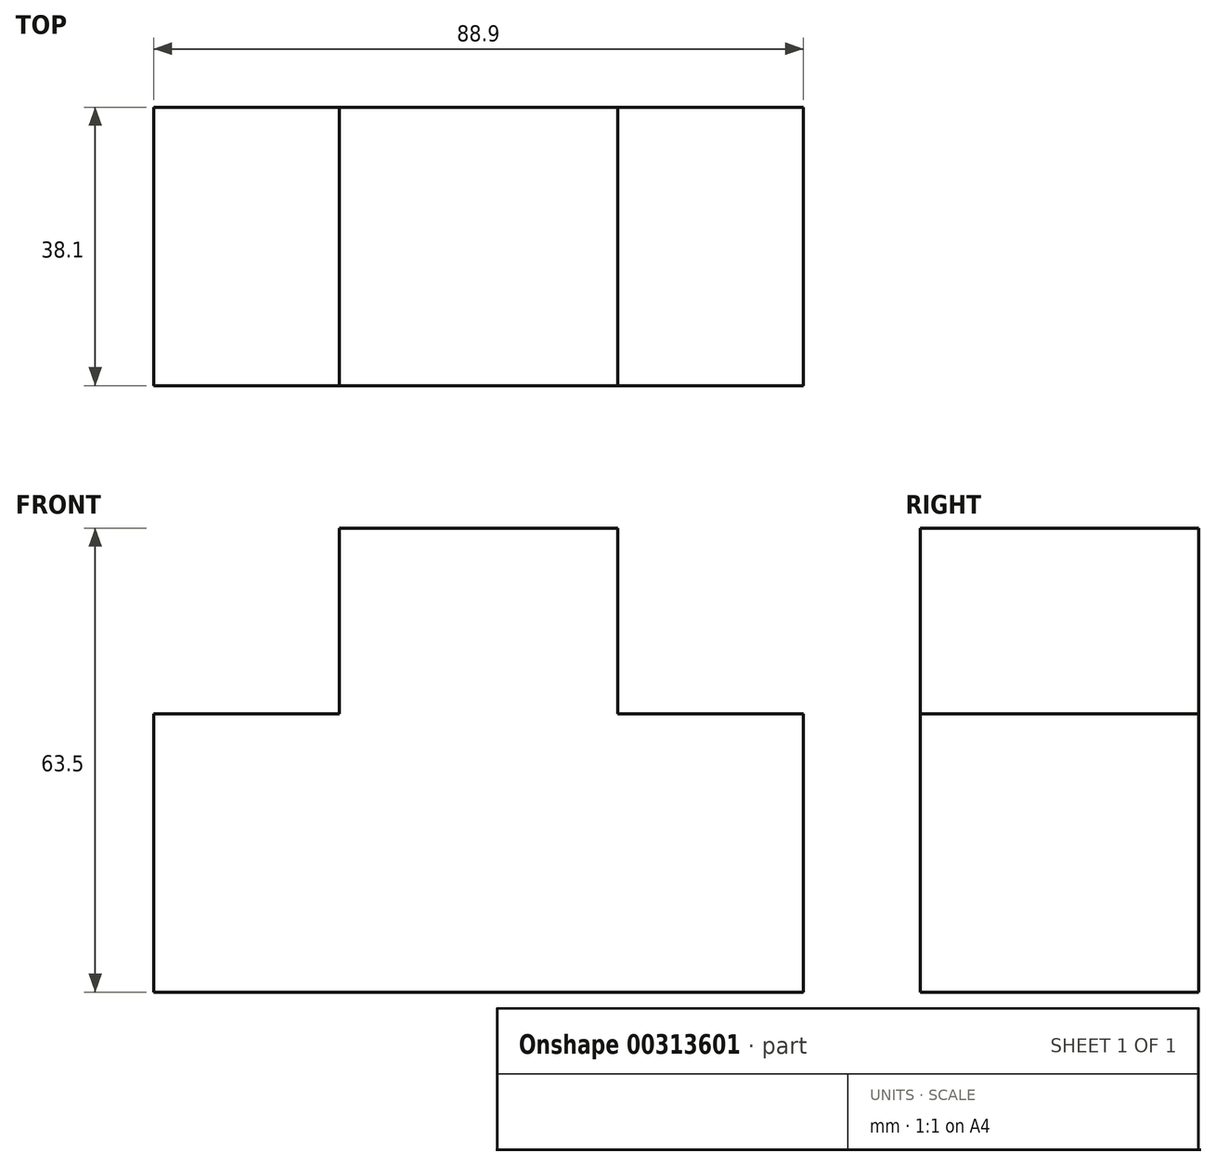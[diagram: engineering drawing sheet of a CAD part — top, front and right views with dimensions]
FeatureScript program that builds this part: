
annotation { "Feature Type Name" : "Feature", "Feature Type Description" : "" }
export const myFeature = defineFeature(function(context is Context, id is Id, definition is map)
    precondition{}
    {
        {
            var Q0;
            Q0=qCreatedBy(makeId("Front.planeOp"),FACE);
            var sketch = newSketch(context, id + "F0", { "sketchPlane" : qUnion([Q0])});
            skLineSegment(sketch, "E0", {"start": v(-52.82, -43.98) * mm, "end": v(36.08, -43.98) * mm});
            skLineSegment(sketch, "E1", {"start": v(36.08, -43.98) * mm, "end": v(36.08, -5.88) * mm});
            skLineSegment(sketch, "E2", {"start": v(36.08, -5.88) * mm, "end": v(10.68, -5.88) * mm});
            skLineSegment(sketch, "E3", {"start": v(10.68, -5.88) * mm, "end": v(10.68, 19.52) * mm});
            skLineSegment(sketch, "E4", {"start": v(10.68, 19.52) * mm, "end": v(-27.42, 19.52) * mm});
            skLineSegment(sketch, "E5", {"start": v(-27.42, 19.52) * mm, "end": v(-27.42, -5.88) * mm});
            skLineSegment(sketch, "E6", {"start": v(-27.42, -5.88) * mm, "end": v(-52.82, -5.88) * mm});
            skLineSegment(sketch, "E7", {"start": v(-52.82, -5.88) * mm, "end": v(-52.82, -43.98) * mm});
            skSolve(sketch);
        }
        {
            var Q0;
            Q0=makeQuery(id+"F0.imprint","IMPRINT",FACE,{"disambiguationData":[TD([[makeQuery(id+"F0.imprint","IMPRINT",EDGE,{"derivedFrom":sQuery(id+"F0.wireOp",EDGE,"E0")}),1.0]])]});
            extrude(context, id + "F1", {"entities" : qUnion([Q0]), "depth" : 38.1 * mm});
        }
    });
